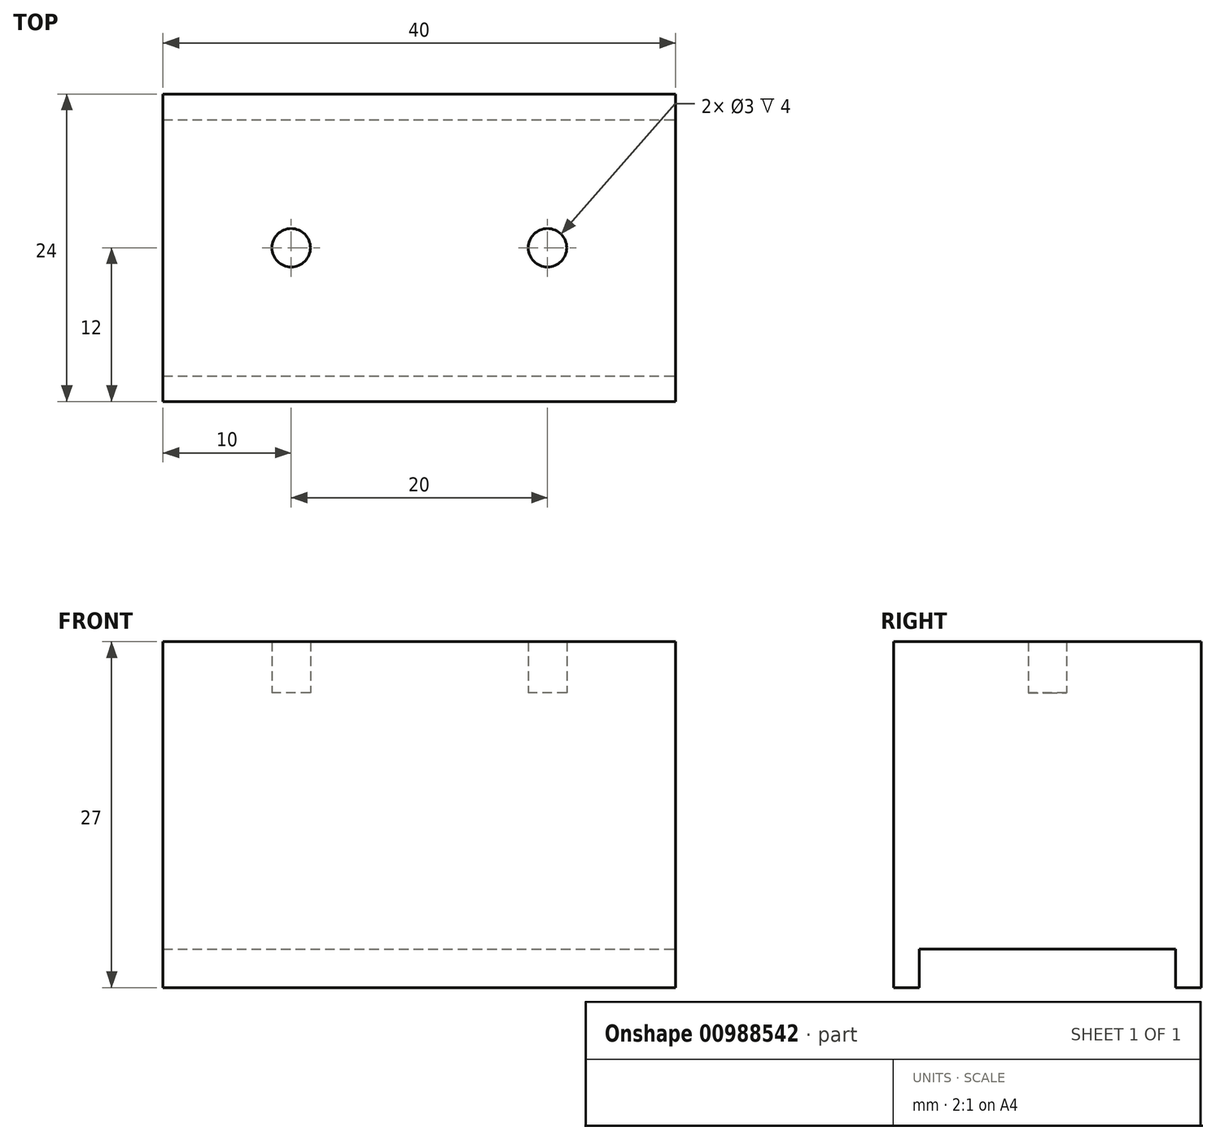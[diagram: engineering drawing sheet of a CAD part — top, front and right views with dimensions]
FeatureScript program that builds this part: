
annotation { "Feature Type Name" : "Feature", "Feature Type Description" : "" }
export const myFeature = defineFeature(function(context is Context, id is Id, definition is map)
    precondition{}
    {
        {
            var Q0;
            Q0=qCreatedBy(makeId("Top.planeOp"),FACE);
            var sketch = newSketch(context, id + "F0", { "sketchPlane" : qUnion([Q0])});
            skLineSegment(sketch, "E0.bottom", {"start": v(-20, 10) * mm, "end": v(20, 10) * mm});
            skLineSegment(sketch, "E0.top", {"start": v(-20, -10) * mm, "end": v(20, -10) * mm});
            skLineSegment(sketch, "E0.left", {"start": v(-20, 10) * mm, "end": v(-20, -10) * mm});
            skLineSegment(sketch, "E0.right", {"start": v(20, 10) * mm, "end": v(20, -10) * mm});
            skPoint(sketch, "E0.middle", {"position": v(0, 0) * mm});
            skSolve(sketch);
        }
        {
            var Q0;
            Q0=makeQuery(id+"F0.imprint","IMPRINT",FACE,{"disambiguationData":[TD([[makeQuery(id+"F0.imprint","IMPRINT",EDGE,{"derivedFrom":sQuery(id+"F0.wireOp",EDGE,"E0.bottom")}),-1.0]])]});
            extrude(context, id + "F1", {"entities" : qUnion([Q0]), "depth" : 20 * mm, "offsetDistance" : 25 * mm});
        }
        {
            var Q0;
            Q0=makeQuery(id+"F1.opExtrude","CAP_FACE",FACE,{"disambiguationData":[OSD([sQuery(id+"F0.wireOp",EDGE,"E0.bottom"),sQuery(id+"F0.wireOp",EDGE,"E0.top"),sQuery(id+"F0.wireOp",EDGE,"E0.left"),sQuery(id+"F0.wireOp",EDGE,"E0.right")])],"isStart":false});
            var sketch = newSketch(context, id + "F2", { "sketchPlane" : qUnion([Q0])});
            skLineSegment(sketch, "E1", {"start": v(-10, 10) * mm, "end": v(-10, -10) * mm});
            skLineSegment(sketch, "E2", {"start": v(10, 10) * mm, "end": v(10, -10) * mm});
            skPoint(sketch, "E3", {"position": v(-10, 0) * mm});
            skPoint(sketch, "E4", {"position": v(10, 0) * mm});
            skCircle(sketch, "E5", {"center": v(-10, 0) * mm, "radius": 1.5 * mm});
            skCircle(sketch, "E6", {"center": v(10, 0) * mm, "radius": 1.5 * mm});
            skSolve(sketch);
        }
        {
            var Q0;
            {var subQ0=sQuery(id+"F2.wireOp",EDGE,"E5");var subQ1=sQuery(id+"F2.wireOp",EDGE,"E1");var subQ2=makeQuery(id+"F2.imprint","INTERSECT",VERTEX,{"disambiguationData":[OD(0.0)],"derivedFrom":[subQ1,subQ0]});Q0=makeQuery(id+"F2.imprint","IMPRINT",FACE,{"disambiguationData":[TD([[makeQuery(id+"F2.imprint","IMPRINT",EDGE,{"disambiguationData":[TD([[subQ2,-1.0]])],"derivedFrom":subQ1}),-1.0]])]});}
            var Q1;
            {var subQ0=sQuery(id+"F2.wireOp",EDGE,"E5");var subQ1=sQuery(id+"F2.wireOp",EDGE,"E1");var subQ2=makeQuery(id+"F2.imprint","INTERSECT",VERTEX,{"disambiguationData":[OD(0.0)],"derivedFrom":[subQ1,subQ0]});Q1=makeQuery(id+"F2.imprint","IMPRINT",FACE,{"disambiguationData":[TD([[makeQuery(id+"F2.imprint","IMPRINT",EDGE,{"disambiguationData":[TD([[subQ2,-1.0]])],"derivedFrom":subQ1}),1.0]])]});}
            var Q2;
            {var subQ0=sQuery(id+"F2.wireOp",EDGE,"E6");var subQ1=sQuery(id+"F2.wireOp",EDGE,"E2");var subQ2=makeQuery(id+"F2.imprint","INTERSECT",VERTEX,{"disambiguationData":[OD(0.0)],"derivedFrom":[subQ1,subQ0]});Q2=makeQuery(id+"F2.imprint","IMPRINT",FACE,{"disambiguationData":[TD([[makeQuery(id+"F2.imprint","IMPRINT",EDGE,{"disambiguationData":[TD([[subQ2,-1.0]])],"derivedFrom":subQ1}),-1.0]])]});}
            var Q3;
            {var subQ0=sQuery(id+"F2.wireOp",EDGE,"E6");var subQ1=sQuery(id+"F2.wireOp",EDGE,"E2");var subQ2=makeQuery(id+"F2.imprint","INTERSECT",VERTEX,{"disambiguationData":[OD(0.0)],"derivedFrom":[subQ1,subQ0]});Q3=makeQuery(id+"F2.imprint","IMPRINT",FACE,{"disambiguationData":[TD([[makeQuery(id+"F2.imprint","IMPRINT",EDGE,{"disambiguationData":[TD([[subQ2,-1.0]])],"derivedFrom":subQ1}),1.0]])]});}
            extrude(context, id + "F3", {"entities" : qUnion([Q0, Q1, Q2, Q3]), "operationType" : NewBodyOperationType.ADD, "depth" : 4 * mm, "offsetDistance" : 25 * mm});
        }
        {
            var Q0;
            Q0=makeQuery(id+"F1.opExtrude","SWEPT_FACE",FACE,{"disambiguationData":[OSD([sQuery(id+"F0.wireOp",EDGE,"E0.top")])]});
            extrude(context, id + "F4", {"entities" : qUnion([Q0]), "operationType" : NewBodyOperationType.ADD, "depth" : 2 * mm, "offsetDistance" : 25 * mm});
        }
        {
            var Q0;
            Q0=makeQuery(id+"F1.opExtrude","SWEPT_FACE",FACE,{"disambiguationData":[OSD([sQuery(id+"F0.wireOp",EDGE,"E0.bottom")])]});
            extrude(context, id + "F5", {"entities" : qUnion([Q0]), "operationType" : NewBodyOperationType.ADD, "depth" : 2 * mm, "offsetDistance" : 25 * mm});
        }
        {
            var Q0;
            {var subQ0=sQuery(id+"F0.wireOp",EDGE,"E0.bottom");var subQ1=sQuery(id+"F0.wireOp",EDGE,"E0.top");Q0=makeQuery(id+"F5.boolean.opBoolean","MERGE",FACE,{"derivedFrom":[makeQuery(id+"F4.boolean.opBoolean","MERGE",FACE,{"derivedFrom":[makeQuery(id+"F1.opExtrude","CAP_FACE",FACE,{"disambiguationData":[OSD([subQ0,subQ1,sQuery(id+"F0.wireOp",EDGE,"E0.left"),sQuery(id+"F0.wireOp",EDGE,"E0.right")])],"isStart":true}),makeQuery(id+"F4.opExtrude","SWEPT_FACE",FACE,{"disambiguationData":[OSD([subQ1]),TDD([makeQuery(id+"F1.opExtrude","CAP_EDGE",EDGE,{"disambiguationData":[OSD([subQ1])],"isStart":true})])]})]}),makeQuery(id+"F5.opExtrude","SWEPT_FACE",FACE,{"disambiguationData":[OSD([subQ0]),TDD([makeQuery(id+"F1.opExtrude","CAP_EDGE",EDGE,{"disambiguationData":[OSD([subQ0])],"isStart":true})])]})]});}
            var sketch = newSketch(context, id + "F6", { "sketchPlane" : qUnion([Q0])});
            skLineSegment(sketch, "E7.bottom", {"start": v(-20, 12) * mm, "end": v(20, 12) * mm});
            skLineSegment(sketch, "E7.top", {"start": v(-20, 10) * mm, "end": v(20, 10) * mm});
            skLineSegment(sketch, "E7.left", {"start": v(-20, 12) * mm, "end": v(-20, 10) * mm});
            skLineSegment(sketch, "E7.right", {"start": v(20, 12) * mm, "end": v(20, 10) * mm});
            skLineSegment(sketch, "E8.bottom", {"start": v(-20, -12) * mm, "end": v(20, -12) * mm});
            skLineSegment(sketch, "E8.top", {"start": v(-20, -10) * mm, "end": v(20, -10) * mm});
            skLineSegment(sketch, "E8.left", {"start": v(-20, -12) * mm, "end": v(-20, -10) * mm});
            skLineSegment(sketch, "E8.right", {"start": v(20, -12) * mm, "end": v(20, -10) * mm});
            skSolve(sketch);
        }
        {
            var Q0;
            Q0=makeQuery(id+"F6.imprint","IMPRINT",FACE,{"disambiguationData":[TD([[makeQuery(id+"F6.imprint","IMPRINT",EDGE,{"derivedFrom":sQuery(id+"F6.wireOp",EDGE,"E7.bottom")}),-1.0]])]});
            var Q1;
            Q1=makeQuery(id+"F6.imprint","IMPRINT",FACE,{"disambiguationData":[TD([[makeQuery(id+"F6.imprint","IMPRINT",EDGE,{"derivedFrom":sQuery(id+"F6.wireOp",EDGE,"E8.bottom")}),1.0]])]});
            extrude(context, id + "F7", {"entities" : qUnion([Q0, Q1]), "operationType" : NewBodyOperationType.ADD, "depth" : 3 * mm, "offsetDistance" : 25 * mm});
        }
    });
